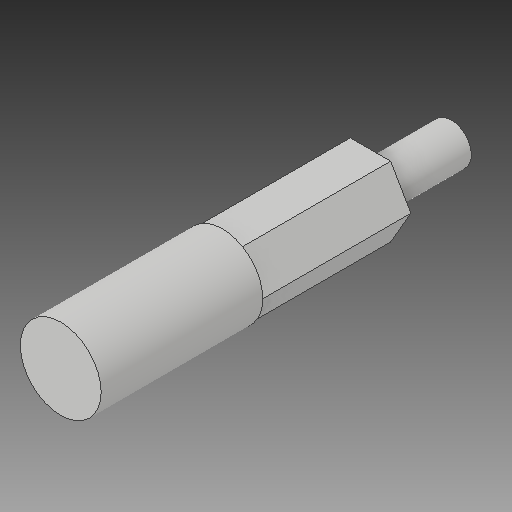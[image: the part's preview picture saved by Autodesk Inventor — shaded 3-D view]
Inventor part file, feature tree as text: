
AUTODESK INVENTOR PART (.ipt)
format: ipt  version: 2019 (Build 230136000, 136)  size: 103,936 bytes
history: native  units: in
note: dims shown in document units (in); Inventor stores cm internally (conversion verified against a paired STEP export)
features: sketch x4, other x3
ambient origin geometry x8: Origin, YZ Plane, XZ Plane, XY Plane, X Axis, Y Axis, Z Axis, Center Point
bodies: Solid1 (feature_tree)
feature tree (7):
  other  "Front_Wheel_Attachment.ipt"
  other  "Solid1::Front_Wheel_Attachment.ipt"
  other  "TaggingFeature1"
  sketch  "Sketch1"  dims[d0=0.3937in]
  sketch  "Sketch2"
  sketch  "Sketch3"
  sketch  "Sketch4"
